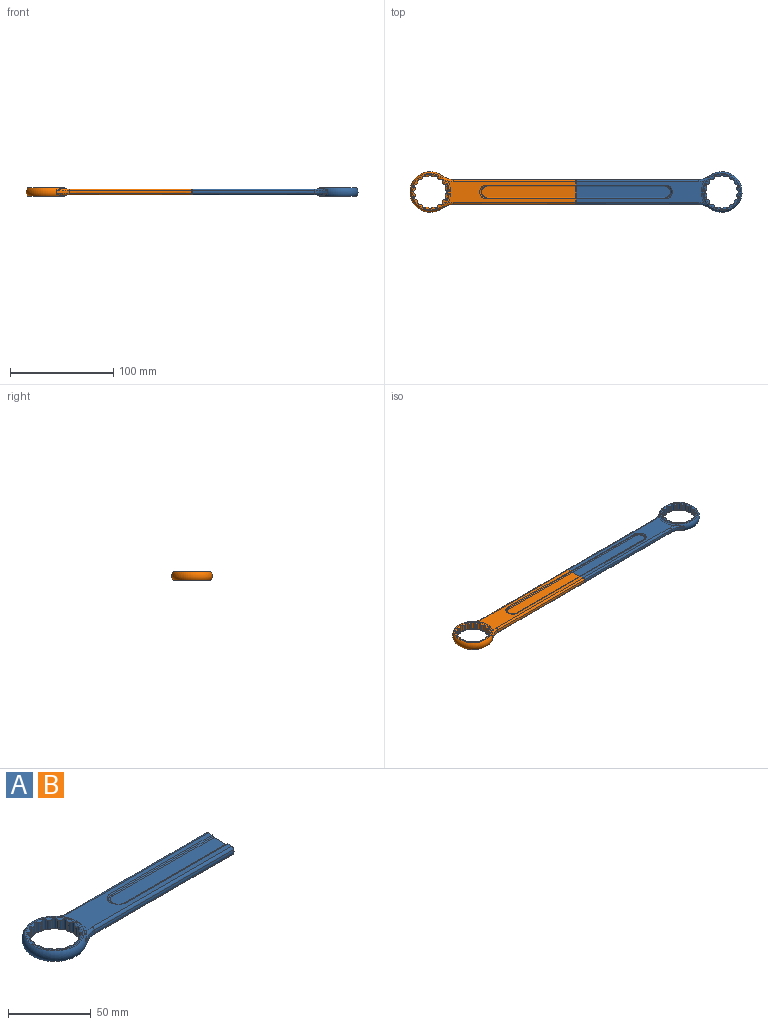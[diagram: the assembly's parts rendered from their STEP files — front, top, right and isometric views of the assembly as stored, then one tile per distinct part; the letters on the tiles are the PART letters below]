
ASSEMBLY  parts=2 mates=1
PART A: 97 faces, bbox 162.5x42.5x9.7 mm
  f0: cylinder r=15mm len=6.23mm, axis (0,0,1), area 3mm2, adj f34,f35,f88,f89
  f1: cylinder r=15mm len=6.23mm, axis (0,0,1), area 3mm2, adj f36,f37,f88,f89
  f2: cylinder r=15mm len=6.23mm, axis (0,0,1), area 3mm2, adj f38,f39,f88,f89
  f3: cylinder r=15mm len=6.23mm, axis (0,0,1), area 3mm2, adj f40,f41,f88,f89
  f4: cylinder r=15mm len=6.23mm, axis (0,0,1), area 3mm2, adj f42,f43,f88,f89
  f5: cylinder r=15mm len=6.23mm, axis (0,0,1), area 3mm2, adj f44,f45,f88,f89
  f6: cylinder r=15mm len=6.23mm, axis (0,0,1), area 3mm2, adj f46,f47,f88,f89
  f7: cylinder r=15mm len=6.23mm, axis (0,0,1), area 3mm2, adj f48,f49,f88,f89
  f8: cylinder r=15mm len=6.23mm, axis (0,0,1), area 3mm2, adj f50,f51,f88,f89
  f9: cylinder r=15mm len=6.23mm, axis (0,0,1), area 3mm2, adj f52,f53,f88,f89
  f10: cylinder r=15mm len=6.23mm, axis (0,0,1), area 3mm2, adj f54,f55,f88,f89
  f11: cylinder r=15mm len=6.23mm, axis (0,0,1), area 3mm2, adj f56,f57,f88,f89
  f12: cylinder r=15mm len=6.23mm, axis (0,0,1), area 3mm2, adj f58,f59,f88,f89
  f13: cylinder r=15mm len=6.23mm, axis (0,0,1), area 3mm2, adj f60,f61,f88,f89
  f14: cylinder r=15mm len=6.23mm, axis (0,0,1), area 3mm2, adj f62,f63,f88,f89
  f15: plane 36x36mm, normal (0,0,1), area 109.4mm2, adj f66,f88
  f16: cylinder r=15mm len=6.23mm, axis (0,0,1), area 3mm2, adj f33,f64,f88,f89
  f17: cylinder r=1.5mm len=7.4mm, axis (0,0,1), area 23.4mm2, adj f63,f64,f88,f89
  f18: cylinder r=1.5mm len=7.4mm, axis (0,0,1), area 23.4mm2, adj f61,f62,f88,f89
  f19: cylinder r=1.5mm len=7.4mm, axis (0,0,1), area 23.4mm2, adj f59,f60,f88,f89
  f20: cylinder r=1.5mm len=7.4mm, axis (0,0,1), area 23.4mm2, adj f57,f58,f88,f89
  f21: cylinder r=1.5mm len=7.4mm, axis (0,0,1), area 23.4mm2, adj f55,f56,f88,f89
  f22: cylinder r=1.5mm len=7.4mm, axis (0,0,1), area 23.4mm2, adj f53,f54,f88,f89
  f23: cylinder r=1.5mm len=7.4mm, axis (0,0,1), area 23.4mm2, adj f51,f52,f88,f89
  f24: cylinder r=1.5mm len=7.4mm, axis (0,0,1), area 23.4mm2, adj f49,f50,f88,f89
  f25: cylinder r=1.5mm len=7.4mm, axis (0,0,1), area 23.4mm2, adj f47,f48,f88,f89
  f26: cylinder r=1.5mm len=7.4mm, axis (0,0,1), area 23.4mm2, adj f45,f46,f88,f89
  f27: cylinder r=1.5mm len=7.4mm, axis (0,0,1), area 23.4mm2, adj f43,f44,f88,f89
  f28: cylinder r=1.5mm len=7.4mm, axis (0,0,1), area 23.4mm2, adj f41,f42,f88,f89
  f29: cylinder r=1.5mm len=7.4mm, axis (0,0,1), area 23.4mm2, adj f39,f40,f88,f89
  f30: cylinder r=1.5mm len=7.4mm, axis (0,0,1), area 23.4mm2, adj f37,f38,f88,f89
  f31: cylinder r=1.5mm len=7.4mm, axis (0,0,1), area 23.4mm2, adj f35,f36,f88,f89
  f32: cylinder r=1.5mm len=7.4mm, axis (0,0,1), area 23.4mm2, adj f33,f34,f88,f89
  f33: cylinder r=2mm len=7.4mm, axis (0,0,1), area 11.9mm2, adj f16,f32,f88,f89
  f34: cylinder r=2mm len=7.4mm, axis (0,0,1), area 11.9mm2, adj f0,f32,f88,f89
  f35: cylinder r=2mm len=7.4mm, axis (0,0,1), area 11.9mm2, adj f0,f31,f88,f89
  f36: cylinder r=2mm len=7.4mm, axis (0,0,1), area 11.9mm2, adj f1,f31,f88,f89
  f37: cylinder r=2mm len=7.4mm, axis (0,0,1), area 11.9mm2, adj f1,f30,f88,f89
  f38: cylinder r=2mm len=7.4mm, axis (0,0,1), area 11.9mm2, adj f2,f30,f88,f89
  f39: cylinder r=2mm len=7.4mm, axis (0,0,1), area 11.9mm2, adj f2,f29,f88,f89
  f40: cylinder r=2mm len=7.4mm, axis (0,0,1), area 11.9mm2, adj f3,f29,f88,f89
  f41: cylinder r=2mm len=7.4mm, axis (0,0,1), area 11.9mm2, adj f3,f28,f88,f89
  f42: cylinder r=2mm len=7.4mm, axis (0,0,1), area 11.9mm2, adj f4,f28,f88,f89
  f43: cylinder r=2mm len=7.4mm, axis (0,0,1), area 11.9mm2, adj f4,f27,f88,f89
  f44: cylinder r=2mm len=7.4mm, axis (0,0,1), area 11.9mm2, adj f5,f27,f88,f89
  f45: cylinder r=2mm len=7.4mm, axis (0,0,1), area 11.9mm2, adj f5,f26,f88,f89
  f46: cylinder r=2mm len=7.4mm, axis (0,0,1), area 11.9mm2, adj f6,f26,f88,f89
  f47: cylinder r=2mm len=7.4mm, axis (0,0,1), area 11.9mm2, adj f6,f25,f88,f89
  f48: cylinder r=2mm len=7.4mm, axis (0,0,1), area 11.9mm2, adj f7,f25,f88,f89
  f49: cylinder r=2mm len=7.4mm, axis (0,0,1), area 11.9mm2, adj f7,f24,f88,f89
  f50: cylinder r=2mm len=7.4mm, axis (0,0,1), area 11.9mm2, adj f8,f24,f88,f89
  f51: cylinder r=2mm len=7.4mm, axis (0,0,1), area 11.9mm2, adj f8,f23,f88,f89
  f52: cylinder r=2mm len=7.4mm, axis (0,0,1), area 11.9mm2, adj f9,f23,f88,f89
  f53: cylinder r=2mm len=7.4mm, axis (0,0,1), area 11.9mm2, adj f9,f22,f88,f89
  f54: cylinder r=2mm len=7.4mm, axis (0,0,1), area 11.9mm2, adj f10,f22,f88,f89
  f55: cylinder r=2mm len=7.4mm, axis (0,0,1), area 11.9mm2, adj f10,f21,f88,f89
  f56: cylinder r=2mm len=7.4mm, axis (0,0,1), area 11.9mm2, adj f11,f21,f88,f89
  f57: cylinder r=2mm len=7.4mm, axis (0,0,1), area 11.9mm2, adj f11,f20,f88,f89
  f58: cylinder r=2mm len=7.4mm, axis (0,0,1), area 11.9mm2, adj f12,f20,f88,f89
  f59: cylinder r=2mm len=7.4mm, axis (0,0,1), area 11.9mm2, adj f12,f19,f88,f89
  f60: cylinder r=2mm len=7.4mm, axis (0,0,1), area 11.9mm2, adj f13,f19,f88,f89
  f61: cylinder r=2mm len=7.4mm, axis (0,0,1), area 11.9mm2, adj f13,f18,f88,f89
  f62: cylinder r=2mm len=7.4mm, axis (0,0,1), area 11.9mm2, adj f14,f18,f88,f89
  f63: cylinder r=2mm len=7.4mm, axis (0,0,1), area 11.9mm2, adj f14,f17,f88,f89
  f64: cylinder r=2mm len=7.4mm, axis (0,0,1), area 11.9mm2, adj f16,f17,f88,f89
  f65: plane 36x36mm, normal (0,0,-1), area 109.4mm2, adj f66,f89
  f66: torus R=13.92mm, axis (0,0,1), area 783.8mm2, adj f15,f65,f69,f70,f75,f76,f77,f78
  f67: plane 124.59x21.88mm, normal (0,0,1), area 1186.7mm2, adj f71,f73,f79,f81,f86,f87,f94,f95
  f68: plane 124.58x21.88mm, normal (0,0,-1), area 2424.5mm2, adj f72,f74,f76,f83,f84,f87
  f69: bspline ~12.77x5.72mm, area 37.3mm2, adj f66,f72,f73,f77,f80,f85
  f70: bspline ~12.77x5.72mm, area 37.3mm2, adj f66,f71,f74,f75,f78,f82
  f71: bspline ~14.87x7.3mm, area 24.2mm2, adj f67,f70,f78,f81
  f72: bspline ~14.59x7.38mm, area 24.2mm2, adj f68,f69,f77,f84
  f73: bspline ~14.86x7.28mm, area 24.2mm2, adj f67,f69,f80,f86
  f74: bspline ~14.58x7.36mm, area 24.2mm2, adj f68,f70,f75,f83
  f75: bspline ~6.4x6.1mm, area 6.8mm2, adj f66,f70,f74,f76
  f76: torus R=19.91mm, axis (0,0,1), area 39.5mm2, adj f66,f68,f75,f77
  f77: bspline ~6.98x6.59mm, area 6.8mm2, adj f66,f69,f72,f76
  f78: bspline ~6.98x6.59mm, area 6.8mm2, adj f66,f70,f71,f79
  f79: torus R=19.91mm, axis (0,0,1), area 39.5mm2, adj f66,f67,f78,f80
  f80: bspline ~6.4x6.1mm, area 6.8mm2, adj f66,f69,f73,f79
  f81: extruded ~119x1.95mm, area 319.5mm2, adj f67,f71,f82,f87
  f82: extruded ~119x2.63mm, area 315.3mm2, adj f70,f81,f83,f87
  f83: extruded ~119x1.95mm, area 319.4mm2, adj f68,f74,f82,f87
  f84: extruded ~119x1.95mm, area 319.5mm2, adj f68,f72,f85,f87
  f85: extruded ~119x2.63mm, area 315.3mm2, adj f69,f84,f86,f87
  f86: extruded ~119x1.95mm, area 319.4mm2, adj f67,f73,f85,f87
  f87: plane 24.03x5.72mm, normal (1,0,0), area 121.3mm2, adj f67,f68,f81,f82,f83,f84,f85,f86
  f88: torus R=17.08mm, axis (0,0,1), area 139.1mm2, adj f0,f1,f2,f3,f4,f5,f6,f7
  f89: torus R=17.08mm, axis (0,0,1), area 139.1mm2, adj f0,f1,f2,f3,f4,f5,f6,f7
  f90: plane 91.65x10mm, normal (0,0,1), area 905.8mm2, adj f87,f91,f92,f93
  f91: cylinder r=1mm len=86.65mm, axis (1,0,0), area 90.7mm2, adj f87,f90,f92,f94
  f92: torus R=5mm, axis (0,0,1), area 18mm2, adj f90,f91,f93,f95
  f93: cylinder r=1mm len=86.65mm, axis (-1,0,0), area 90.7mm2, adj f87,f90,f92,f96
  f94: cylinder r=1mm len=86.65mm, axis (1,0,0), area 90.7mm2, adj f67,f87,f91,f95
  f95: torus R=6.73mm, axis (0,0,1), area 20.6mm2, adj f67,f92,f94,f96
  f96: cylinder r=1mm len=86.65mm, axis (-1,0,0), area 90.7mm2, adj f67,f87,f93,f95
PART B: same geometry as A
PLACE A rot(axis=(0,0,1),180deg) t=(256.67,16.95,-4.91)mm
PLACE B t=(-25.77,16.95,-4.91)mm
MATE fastened A.f87 <-> B.f87  axis (-1,0,0) through (115.45,16.95,-5.14)mm
